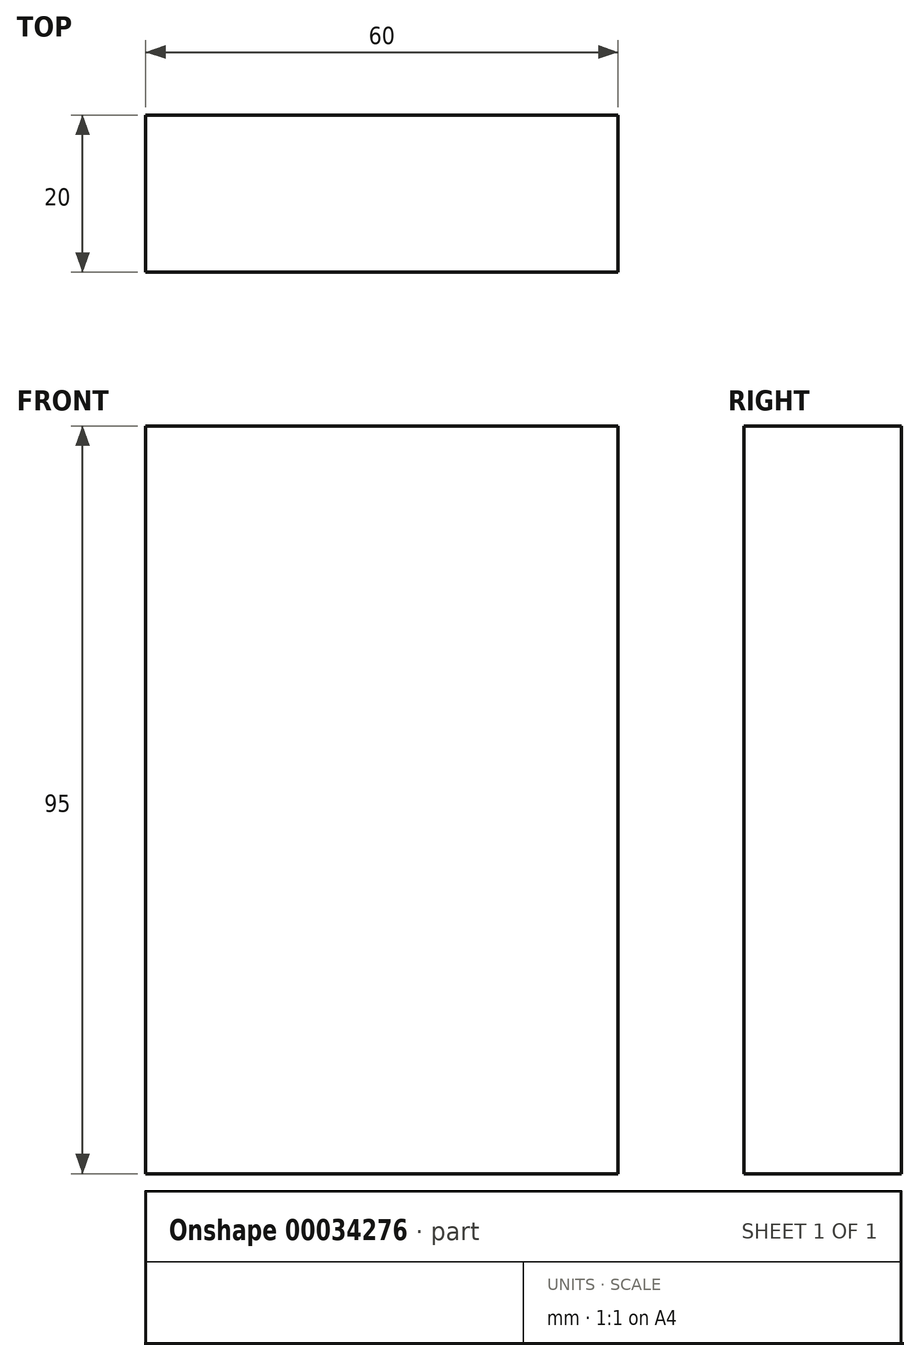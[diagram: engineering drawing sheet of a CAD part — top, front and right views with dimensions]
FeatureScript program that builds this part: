
annotation { "Feature Type Name" : "Feature", "Feature Type Description" : "" }
export const myFeature = defineFeature(function(context is Context, id is Id, definition is map)
    precondition{}
    {
        {
            var Q0;
            Q0=qCreatedBy(makeId("Front.planeOp"),FACE);
            var sketch = newSketch(context, id + "F0", { "sketchPlane" : qUnion([Q0])});
            skLineSegment(sketch, "E0.bottom", {"start": v(-27.65, 56.62) * mm, "end": v(32.35, 56.62) * mm});
            skLineSegment(sketch, "E0.top", {"start": v(-27.65, -38.38) * mm, "end": v(32.35, -38.38) * mm});
            skLineSegment(sketch, "E0.left", {"start": v(-27.65, 56.62) * mm, "end": v(-27.65, -38.38) * mm});
            skLineSegment(sketch, "E0.right", {"start": v(32.35, 56.62) * mm, "end": v(32.35, -38.38) * mm});
            skSolve(sketch);
        }
        {
            var Q0;
            Q0 = qSketchRegion(id + "F0", true);
            extrude(context, id + "F1", {"entities" : qUnion([Q0]), "depth" : 20 * mm});
        }
    });
